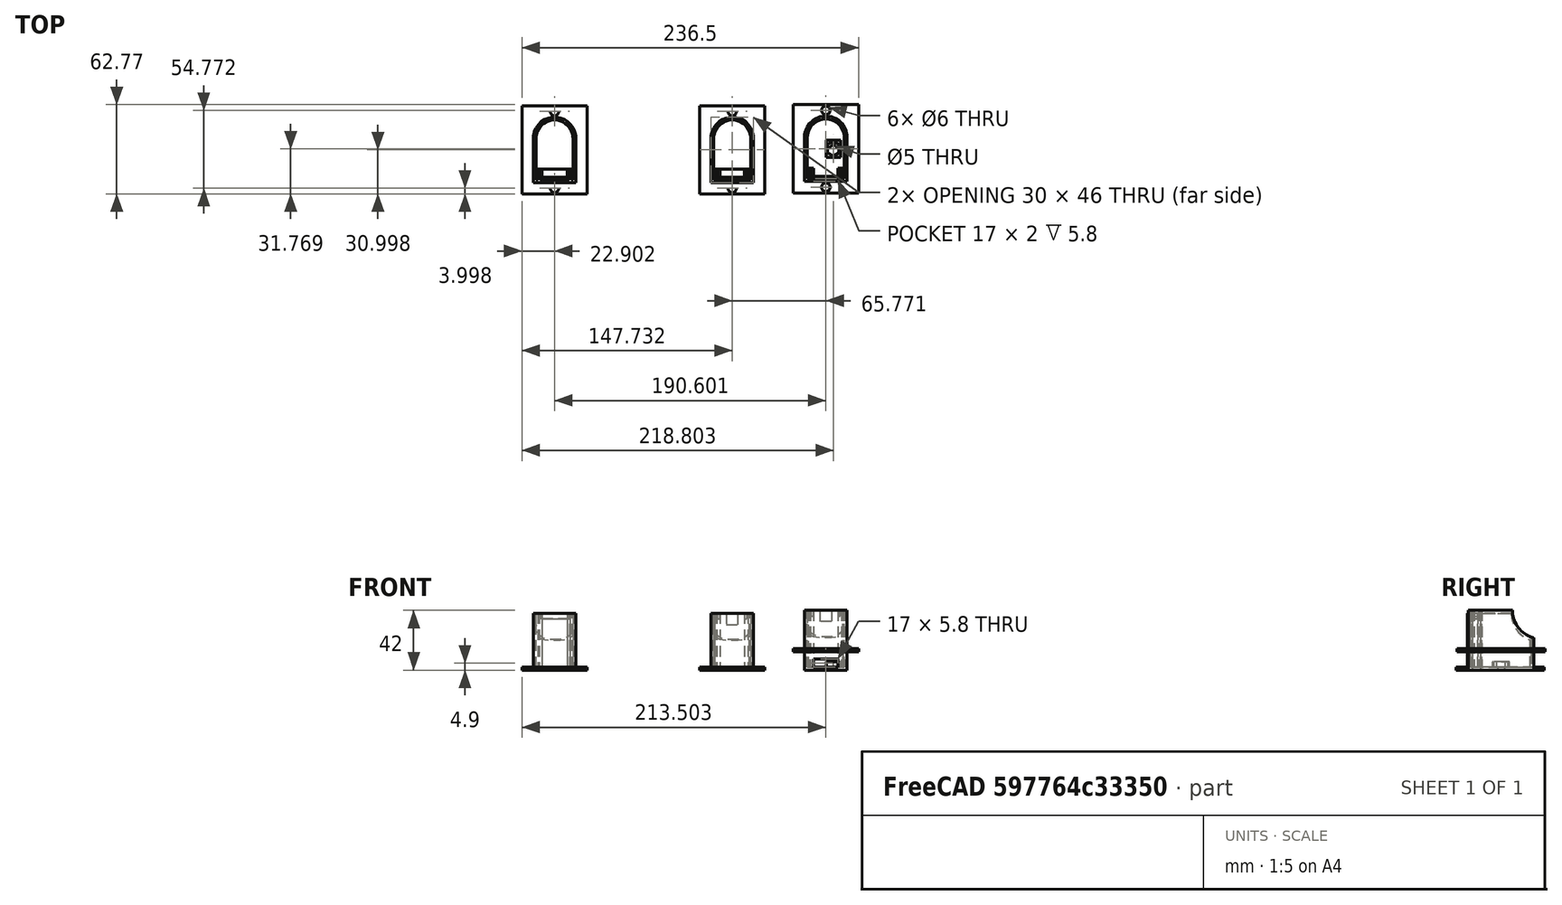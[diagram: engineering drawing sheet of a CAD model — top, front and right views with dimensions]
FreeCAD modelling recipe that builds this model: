
FCSTD DOCUMENT  (FreeCAD 0.18.3R)
Label: lamp.base.nest
License: All rights reserved
LicenseURL: http://en.wikipedia.org/wiki/All_rights_reserved
objects: Part::Extrusion×53, Part::Part2DObjectPython×37, Part::Cut×32, Part::Feature×18, Part::MultiFuse×16, Part::FeaturePython×4
note: 160 computed .brp shape members not serialized (recipe doc carries the construction recipe); baked Part::Feature solids carry a one-line shape summary decoded from their .brp

FEATURE [Part::Part2DObjectPython] Rectangle101  # Draft 2D object (typed FeaturePython)
  ChamferSize = 0
  Columns = 1
  FilletRadius = 0
  Height = 31
  Length = 30
  MakeFace = true
  Placement = pos=(159.976,-36.4369,7.33666) rot=(-1,0,0;2.2e-05rad)
  Rows = 1
FEATURE [Part::Part2DObjectPython] Wire004  # Draft 2D object (typed FeaturePython)
  ChamferSize = 0
  Closed = true
  End = (187.476,-29.036,47.3366)
  FilletRadius = 0
  Length = 82.5995
  MakeFace = true
  Placement = pos=(187.476,-27.0365,47.3366) rot=(1,0,0;3.14159rad)
  Points = (16) [(0,0,0),(-4,-0.000548196,-3.55271e-15),(-4,5.79945,-3.55271e-15),(-21,5.79945,0),(-21,-0.000548196,0),(-25,-0.000548196,3.55271e-15),+10 more]
  Start = (187.476,-27.0365,47.3366)
  Subdivisions = 0
FEATURE [Part::Part2DObjectPython] Circle011  # Draft 2D object (typed FeaturePython)
  FirstAngle = 0
  LastAngle = 0
  MakeFace = true
  Placement = pos=(174.976,-5.43685,7.33598) rot=(-1,0,0;2.2e-05rad)
  Radius = 15
FEATURE [Part::Extrusion] Extrude138
  Base = -> Circle011
  Dir = (0,2.19278e-05,1)
  DirMode = 2
  FaceMakerClass = Part::FaceMakerBullseye
  LengthFwd = 40
  LengthRev = 0
  Solid = false
  Symmetric = false
FEATURE [Part::Extrusion] Extrusion
  Base = -> Wire004
  Dir = (4.1e-15,2.69e-14,-40)
  DirMode = 0
  FaceMakerClass = Part::FaceMakerBullseye
  LengthFwd = 0
  LengthRev = 0
  Solid = true
  Symmetric = false
FEATURE [Part::Part2DObjectPython] Rectangle103  # Draft 2D object (typed FeaturePython)
  ChamferSize = 0
  Columns = 1
  FilletRadius = 0
  Height = 29
  Length = 26
  MakeFace = true
  Placement = pos=(161.976,-34.4369,7.33661) rot=(-1,0,0;2.2e-05rad)
  Rows = 1
FEATURE [Part::Part2DObjectPython] Circle008  # Draft 2D object (typed FeaturePython)
  FirstAngle = 0
  LastAngle = 0
  MakeFace = true
  Placement = pos=(174.976,-5.43685,7.33598) rot=(-1,0,0;2.2e-05rad)
  Radius = 13
FEATURE [Part::Extrusion] Extrude137
  Base = -> Circle008
  Dir = (0,2.19278e-05,1)
  DirMode = 2
  FaceMakerClass = Part::FaceMakerBullseye
  LengthFwd = 40
  LengthRev = 0
  Solid = false
  Symmetric = false
FEATURE [Part::Cut] Cut046
  Base = -> Extrude138
  Tool = -> Extrude137
FEATURE [Part::Extrusion] Extrude136
  Base = -> Rectangle101
  Dir = (0,2.19278e-05,1)
  DirMode = 2
  FaceMakerClass = Part::FaceMakerBullseye
  LengthFwd = 40
  LengthRev = 0
  Solid = false
  Symmetric = false
FEATURE [Part::Extrusion] Extrude129
  Base = -> Rectangle103
  Dir = (0,2.19278e-05,1)
  DirMode = 2
  FaceMakerClass = Part::FaceMakerBullseye
  LengthFwd = 40
  LengthRev = 0
  Solid = false
  Symmetric = false
FEATURE [Part::Cut] Cut045
  Base = -> Extrude136
  Tool = -> Extrude129
FEATURE [Part::Part2DObjectPython] Rectangle102  # Draft 2D object (typed FeaturePython)
  ChamferSize = 0
  Columns = 1
  FilletRadius = 0
  Height = 30
  Length = 40
  MakeFace = true
  Placement = pos=(159.976,-5.43685,7.33598) rot=(0.577354,0.577354,0.577342;4.18878rad)
  Rows = 1
  Support = -> [Cut045]
FEATURE [Part::FeaturePython] Slice001  # WARN: FeaturePython — macro-defined, semantics opaque (R4)
  Base = -> Cut046
  Mode = 1
  Tolerance = 0
  Tools = -> [Rectangle102]
FEATURE [Part::FeaturePython] Slice_child001  label="Slice.001"  # WARN: FeaturePython — macro-defined, semantics opaque (R4)
  Base = -> Slice001
  FilterType = 1
  Invert = false
  OverrideMaxVal = 0
  Placement = pos=(56.3169,21.6057,-20.0005) rot=(0,0,1;0rad)
  WindowFrom = 80
  WindowTo = 100
  items = 0
FEATURE [Part::Part2DObjectPython] Circle012  # Draft 2D object (typed FeaturePython)
  FirstAngle = 0
  LastAngle = 0
  MakeFace = true
  Placement = pos=(159.976,95.9163,14.9502) rot=(0.577346,-0.577359,-0.577346;2.09438rad)
  Radius = 20
  Support = -> [Cut045]
FEATURE [Part::Extrusion] Extrude139
  Base = -> Circle012
  Dir = (-1,-1e-16,1e-16)
  DirMode = 2
  FaceMakerClass = Part::FaceMakerBullseye
  LengthFwd = 50
  LengthRev = 0
  Placement = pos=(106.317,-59.7466,12.3849) rot=(0,0,1;0rad)
  Solid = false
  Symmetric = false
FEATURE [Part::Cut] Cut047
  Base = -> Slice_child001
  Placement = pos=(-56.3169,-21.6057,20.0005) rot=(0,0,1;0rad)
  Tool = -> Extrude139
FEATURE [Part::MultiFuse] Fusion030
  Shapes = -> [Cut045,Cut047]
FEATURE [Part::MultiFuse] Fusion029
  Placement = pos=(-344.724,-139.426,0.00305731) rot=(0,0,1;0rad)
  Shapes = -> [Extrusion,Fusion030]
FEATURE [Part::Part2DObjectPython] Rectangle  # Draft 2D object (typed FeaturePython)
  ChamferSize = 0
  Columns = 1
  FilletRadius = 0
  Height = 8
  Length = 1
  MakeFace = true
  Placement = pos=(-182.748,-173.862,47.3397) rot=(-1,0,0;2.2e-05rad)
  Rows = 1
  Support = -> [Fusion029]
FEATURE [Part::Extrusion] Extrude
  Base = -> Rectangle
  Dir = (0,2.19278e-05,1)
  DirMode = 2
  FaceMakerClass = Part::FaceMakerBullseye
  LengthFwd = -60
  LengthRev = 0
  Placement = pos=(0,0.000219278,10) rot=(0,0,1;0rad)
  Solid = false
  Symmetric = false
FEATURE [Part::Cut] Cut050
  Base = -> Fusion029
  Tool = -> Extrude
FEATURE [Part::Part2DObjectPython] Rectangle105  # Draft 2D object (typed FeaturePython)
  ChamferSize = 0
  Columns = 1
  FilletRadius = 0
  Height = 8
  Length = 1
  MakeFace = true
  Placement = pos=(-157.248,-173.862,47.3397) rot=(-1,0,0;2.2e-05rad)
  Rows = 1
  Support = -> [Cut050]
FEATURE [Part::Extrusion] Extrude144
  Base = -> Rectangle105
  Dir = (0,2.19278e-05,1)
  DirMode = 2
  FaceMakerClass = Part::FaceMakerBullseye
  LengthFwd = -60
  LengthRev = 0
  Placement = pos=(-0.5,0.000219278,10) rot=(0,0,1;0rad)
  Solid = false
  Symmetric = false
FEATURE [Part::Cut] Cut051
  Base = -> Cut050
  Tool = -> Extrude144
FEATURE [Part::Part2DObjectPython] Rectangle106  # Draft 2D object (typed FeaturePython)
  ChamferSize = 0
  Columns = 1
  FilletRadius = 0
  Height = 40
  Length = 2
  MakeFace = true
  Placement = pos=(-157.248,-173.862,7.33967) rot=(0.57735,0.57735,0.57735;2.0944rad)
  Rows = 1
  Support = -> [Cut051]
FEATURE [Part::Extrusion] Extrude145
  Base = -> Rectangle106
  Dir = (1,-7e-16,-7e-16)
  DirMode = 2
  FaceMakerClass = Part::FaceMakerBullseye
  LengthFwd = -0.5
  LengthRev = 0
  Solid = false
  Symmetric = false
FEATURE [Part::Cut] Cut052
  Base = -> Cut051
  Tool = -> Extrude145
FEATURE [Part::Part2DObjectPython] Rectangle107  # Draft 2D object (typed FeaturePython)
  ChamferSize = 0
  Columns = 1
  FilletRadius = 0
  Height = 40
  Length = 2
  MakeFace = true
  Placement = pos=(-182.248,-171.862,7.33967) rot=(0.57735,-0.57735,-0.57735;2.0944rad)
  Rows = 1
  Support = -> [Cut052]
FEATURE [Part::Extrusion] Extrude146
  Base = -> Rectangle107
  Dir = (-1,-2e-16,-3e-16)
  DirMode = 2
  FaceMakerClass = Part::FaceMakerBullseye
  LengthFwd = -0.5
  LengthRev = 0
  Solid = false
  Symmetric = false
FEATURE [Part::Cut] Cut053
  Base = -> Cut052
  Tool = -> Extrude146
FEATURE [Part::Part2DObjectPython] Rectangle108  # Draft 2D object (typed FeaturePython)
  ChamferSize = 0
  Columns = 1
  FilletRadius = 0
  Height = 62
  Length = 46
  MakeFace = true
  Placement = pos=(-192.748,-121.863,7.33853) rot=(1,0,0;3.14157rad)
  Rows = 1
FEATURE [Part::Extrusion] Extrude147
  Base = -> Rectangle108
  Dir = (0,-2.19278e-05,-1)
  DirMode = 2
  FaceMakerClass = Part::FaceMakerBullseye
  LengthFwd = -2
  LengthRev = 0
  Solid = false
  Symmetric = false
FEATURE [Part::Part2DObjectPython] Circle  # Draft 2D object (typed FeaturePython)
  FirstAngle = 0
  LastAngle = 0
  MakeFace = true
  Placement = pos=(-169.748,-125.863,7.33862) rot=(1,0,0;3.14157rad)
  Radius = 3
  Support = -> [Extrude147]
FEATURE [Part::Part2DObjectPython] Circle013  # Draft 2D object (typed FeaturePython)
  FirstAngle = 0
  LastAngle = 0
  MakeFace = true
  Placement = pos=(-169.748,-179.863,7.3398) rot=(1,0,0;3.14157rad)
  Radius = 3
FEATURE [Part::Extrusion] Extrude148
  Base = -> Circle
  Dir = (0,-2.19278e-05,-1)
  DirMode = 2
  FaceMakerClass = Part::FaceMakerBullseye
  LengthFwd = -4
  LengthRev = 0
  Solid = false
  Symmetric = false
FEATURE [Part::Extrusion] Extrude149
  Base = -> Circle013
  Dir = (0,-2.19278e-05,-1)
  DirMode = 2
  FaceMakerClass = Part::FaceMakerBullseye
  LengthFwd = -4
  LengthRev = 0
  Solid = false
  Symmetric = false
FEATURE [Part::Cut] Cut
  Base = -> Extrude147
  Tool = -> Extrude149
FEATURE [Part::Cut] Cut054
  Base = -> Cut
  Tool = -> Extrude148
FEATURE [Part::MultiFuse] Fusion
  Shapes = -> [Cut054,Cut053]
FEATURE [Part::Part2DObjectPython] Rectangle109  # Draft 2D object (typed FeaturePython)
  ChamferSize = 0
  Columns = 1
  FilletRadius = 0
  Height = 5.8
  Length = 17
  MakeFace = true
  Placement = pos=(-178.248,-172.262,9.33964) rot=(-1,0,0;2.2e-05rad)
  Rows = 1
  Support = -> [Fusion]
FEATURE [Part::Extrusion] Extrude150
  Base = -> Rectangle109
  Dir = (0,2.19278e-05,1)
  DirMode = 2
  FaceMakerClass = Part::FaceMakerBullseye
  LengthFwd = -10
  LengthRev = 0
  Solid = false
  Symmetric = false
FEATURE [Part::Cut] Cut055
  Base = -> Fusion
  Tool = -> Extrude150
FEATURE [Part::Part2DObjectPython] Rectangle110  # Draft 2D object (typed FeaturePython)
  ChamferSize = 0
  Columns = 1
  FilletRadius = 0
  Height = 8
  Length = 8
  MakeFace = true
  Placement = pos=(-133.024,-172.269,47.3397) rot=(-1,0,0;1.5708rad)
  Rows = 1
FEATURE [Part::Extrusion] Extrude151
  Base = -> Rectangle110
  Dir = (0,1,7e-16)
  DirMode = 2
  FaceMakerClass = Part::FaceMakerBullseye
  LengthFwd = -1.7
  LengthRev = 0
  Placement = pos=(-40.7237,0.0066316,-3.08384e-05) rot=(0,0,1;0rad)
  Solid = false
  Symmetric = false
FEATURE [Part::Part2DObjectPython] Rectangle111  # Draft 2D object (typed FeaturePython)
  ChamferSize = 0
  Columns = 1
  FilletRadius = 0
  Height = 6.3
  Length = 1.2
  MakeFace = true
  Placement = pos=(-139.224,-173.869,47.3397) rot=(0,0,1;0rad)
  Rows = 1
FEATURE [Part::Feature] Face002
  Placement = pos=(-173.748,-172.262,47.3397) rot=(-1,0,0;1.5708rad)
  shape: bbox 8 x 2e-07 x 8 mm, 1 faces, 0 solids (baked)
FEATURE [Part::Feature] Face004
  shape: bbox 8 x 3.49 x 4.243e-07 mm, 1 faces, 0 solids (baked)
FEATURE [Part::Feature] Face005
  shape: bbox 8 x 1.7 x 2e-07 mm, 1 faces, 0 solids (baked)
FEATURE [Part::Extrusion] Extrude152
  Base = -> Rectangle111
  Dir = (0,-8e-16,1)
  DirMode = 2
  FaceMakerClass = Part::FaceMakerBullseye
  LengthFwd = -4
  LengthRev = 0
  Placement = pos=(-40.7237,0.0066316,-3.08384e-05) rot=(0,0,1;0rad)
  Solid = false
  Symmetric = false
FEATURE [Part::Part2DObjectPython] Rectangle112  # Draft 2D object (typed FeaturePython)
  ChamferSize = 0
  Columns = 1
  FilletRadius = 0
  Height = 6.3
  Length = 1.2
  MakeFace = true
  Placement = pos=(-120.024,-173.869,47.3397) rot=(0,0,1;0rad)
  Rows = 1
FEATURE [Part::Extrusion] Extrude153
  Base = -> Rectangle112
  Dir = (0,-8e-16,1)
  DirMode = 2
  FaceMakerClass = Part::FaceMakerBullseye
  LengthFwd = -4
  LengthRev = 0
  Placement = pos=(-40.7237,0.0066316,-3.08384e-05) rot=(0,0,1;0rad)
  Solid = false
  Symmetric = false
FEATURE [Part::Extrusion] Extrusion004
  Base = -> Face002
  Dir = (1e-16,3.49022,2.7e-15)
  DirMode = 0
  FaceMakerClass = Part::FaceMakerBullseye
  LengthFwd = 0
  LengthRev = 0
  Solid = true
  Symmetric = false
FEATURE [Part::MultiFuse] Fusion032
  Shapes = -> [Extrusion004,Extrude151]
FEATURE [Part::Extrusion] Extrusion005
  Base = -> Face004
  Dir = (3e-16,-7.8e-15,10.0677)
  DirMode = 0
  FaceMakerClass = Part::FaceMakerBullseye
  LengthFwd = 0
  LengthRev = 0
  Solid = true
  Symmetric = false
FEATURE [Part::Extrusion] Extrusion006
  Base = -> Face005
  Dir = (3e-16,-7.3e-15,10.0677)
  DirMode = 0
  FaceMakerClass = Part::FaceMakerBullseye
  LengthFwd = 0
  LengthRev = 0
  Solid = true
  Symmetric = false
FEATURE [Part::MultiFuse] Fusion033
  Shapes = -> [Fusion032,Extrusion006,Extrusion005]
FEATURE [Part::MultiFuse] Fusion034
  Shapes = -> [Fusion033,Extrude153,Extrude152]
FEATURE [Part::Cut] Cut056
  Base = -> Cut055
  Placement = pos=(-6.0896,-2.3491,-1.99694) rot=(0,0,1;0rad)
  Tool = -> Fusion034
FEATURE [Part::Part2DObjectPython] Wire005  # Draft 2D object (typed FeaturePython)
  ChamferSize = 0
  Closed = true
  End = (187.476,-29.036,47.3366)
  FilletRadius = 0
  Length = 82.5995
  MakeFace = true
  Placement = pos=(187.476,-27.0365,47.3366) rot=(1,0,0;3.14159rad)
  Points = (16) [(0,0,0),(-4,-0.000548196,-3.55271e-15),(-4,5.79945,-3.55271e-15),(-21,5.79945,0),(-21,-0.000548196,0),(-25,-0.000548196,3.55271e-15),+10 more]
  Start = (187.476,-27.0365,47.3366)
  Subdivisions = 0
FEATURE [Part::Part2DObjectPython] Circle014  # Draft 2D object (typed FeaturePython)
  FirstAngle = 0
  LastAngle = 0
  MakeFace = true
  Placement = pos=(174.976,-5.43685,7.33598) rot=(-1,0,0;2.2e-05rad)
  Radius = 15
FEATURE [Part::Extrusion] Extrude154
  Base = -> Circle014
  Dir = (0,2.19278e-05,1)
  DirMode = 2
  FaceMakerClass = Part::FaceMakerBullseye
  LengthFwd = 40
  LengthRev = 0
  Solid = false
  Symmetric = false
FEATURE [Part::Part2DObjectPython] Circle015  # Draft 2D object (typed FeaturePython)
  FirstAngle = 0
  LastAngle = 0
  MakeFace = true
  Placement = pos=(174.976,-5.43685,7.33598) rot=(-1,0,0;2.2e-05rad)
  Radius = 13
FEATURE [Part::Part2DObjectPython] Rectangle118  # Draft 2D object (typed FeaturePython)
  ChamferSize = 0
  Columns = 1
  FilletRadius = 0
  Height = 29
  Length = 26
  MakeFace = true
  Placement = pos=(161.976,-34.4369,7.33661) rot=(-1,0,0;2.2e-05rad)
  Rows = 1
FEATURE [Part::Extrusion] Extrusion023
  Base = -> Wire005
  Dir = (4.1e-15,2.69e-14,-40)
  DirMode = 0
  FaceMakerClass = Part::FaceMakerBullseye
  LengthFwd = 0
  LengthRev = 0
  Solid = true
  Symmetric = false
FEATURE [Part::Extrusion] Extrude178
  Base = -> Circle015
  Dir = (0,2.19278e-05,1)
  DirMode = 2
  FaceMakerClass = Part::FaceMakerBullseye
  LengthFwd = 40
  LengthRev = 0
  Solid = false
  Symmetric = false
FEATURE [Part::Cut] Cut062
  Base = -> Extrude154
  Tool = -> Extrude178
FEATURE [Part::Extrusion] Extrude179
  Base = -> Rectangle118
  Dir = (0,2.19278e-05,1)
  DirMode = 2
  FaceMakerClass = Part::FaceMakerBullseye
  LengthFwd = 40
  LengthRev = 0
  Solid = false
  Symmetric = false
FEATURE [Part::Part2DObjectPython] Rectangle119  # Draft 2D object (typed FeaturePython)
  ChamferSize = 0
  Columns = 1
  FilletRadius = 0
  Height = 31
  Length = 30
  MakeFace = true
  Placement = pos=(159.976,-36.4369,7.33666) rot=(-1,0,0;2.2e-05rad)
  Rows = 1
FEATURE [Part::Extrusion] Extrude176
  Base = -> Rectangle119
  Dir = (0,2.19278e-05,1)
  DirMode = 2
  FaceMakerClass = Part::FaceMakerBullseye
  LengthFwd = 40
  LengthRev = 0
  Solid = false
  Symmetric = false
FEATURE [Part::Cut] Cut061
  Base = -> Extrude176
  Tool = -> Extrude179
FEATURE [Part::Part2DObjectPython] Rectangle117  # Draft 2D object (typed FeaturePython)
  ChamferSize = 0
  Columns = 1
  FilletRadius = 0
  Height = 30
  Length = 40
  MakeFace = true
  Placement = pos=(159.976,-5.43685,7.33598) rot=(0.577354,0.577354,0.577342;4.18878rad)
  Rows = 1
  Support = -> [Cut061]
FEATURE [Part::FeaturePython] Slice002  # WARN: FeaturePython — macro-defined, semantics opaque (R4)
  Base = -> Cut062
  Mode = 1
  Tolerance = 0
  Tools = -> [Rectangle117]
FEATURE [Part::FeaturePython] Slice_child002  label="Slice.002"  # WARN: FeaturePython — macro-defined, semantics opaque (R4)
  Base = -> Slice002
  FilterType = 1
  Invert = false
  OverrideMaxVal = 0
  Placement = pos=(56.3169,21.6057,-20.0005) rot=(0,0,1;0rad)
  WindowFrom = 80
  WindowTo = 100
  items = 0
FEATURE [Part::Part2DObjectPython] Circle016  # Draft 2D object (typed FeaturePython)
  FirstAngle = 0
  LastAngle = 0
  MakeFace = true
  Placement = pos=(159.976,95.9163,14.9502) rot=(0.577346,-0.577359,-0.577346;2.09438rad)
  Radius = 20
  Support = -> [Cut061]
FEATURE [Part::Extrusion] Extrude155
  Base = -> Circle016
  Dir = (-1,-1e-16,1e-16)
  DirMode = 2
  FaceMakerClass = Part::FaceMakerBullseye
  LengthFwd = 50
  LengthRev = 0
  Placement = pos=(106.317,-59.7466,12.3849) rot=(0,0,1;0rad)
  Solid = false
  Symmetric = false
FEATURE [Part::Cut] Cut063
  Base = -> Slice_child002
  Placement = pos=(-56.3169,-21.6057,20.0005) rot=(0,0,1;0rad)
  Tool = -> Extrude155
FEATURE [Part::MultiFuse] Fusion031
  Shapes = -> [Cut061,Cut063]
FEATURE [Part::MultiFuse] Fusion036
  Placement = pos=(-344.724,-139.426,0.00305731) rot=(0,0,1;0rad)
  Shapes = -> [Extrusion023,Fusion031]
FEATURE [Part::Part2DObjectPython] Rectangle114  # Draft 2D object (typed FeaturePython)
  ChamferSize = 0
  Columns = 1
  FilletRadius = 0
  Height = 8
  Length = 1
  MakeFace = true
  Placement = pos=(-182.748,-173.862,47.3397) rot=(-1,0,0;2.2e-05rad)
  Rows = 1
  Support = -> [Fusion036]
FEATURE [Part::Extrusion] Extrude174
  Base = -> Rectangle114
  Dir = (0,2.19278e-05,1)
  DirMode = 2
  FaceMakerClass = Part::FaceMakerBullseye
  LengthFwd = -60
  LengthRev = 0
  Placement = pos=(0,0.000219278,10) rot=(0,0,1;0rad)
  Solid = false
  Symmetric = false
FEATURE [Part::Cut] Cut059
  Base = -> Fusion036
  Tool = -> Extrude174
FEATURE [Part::Part2DObjectPython] Rectangle116  # Draft 2D object (typed FeaturePython)
  ChamferSize = 0
  Columns = 1
  FilletRadius = 0
  Height = 8
  Length = 1
  MakeFace = true
  Placement = pos=(-157.248,-173.862,47.3397) rot=(-1,0,0;2.2e-05rad)
  Rows = 1
  Support = -> [Cut059]
FEATURE [Part::Extrusion] Extrude173
  Base = -> Rectangle116
  Dir = (0,2.19278e-05,1)
  DirMode = 2
  FaceMakerClass = Part::FaceMakerBullseye
  LengthFwd = -60
  LengthRev = 0
  Placement = pos=(-0.5,0.000219278,10) rot=(0,0,1;0rad)
  Solid = false
  Symmetric = false
FEATURE [Part::Cut] Cut058
  Base = -> Cut059
  Tool = -> Extrude173
FEATURE [Part::Part2DObjectPython] Rectangle115  # Draft 2D object (typed FeaturePython)
  ChamferSize = 0
  Columns = 1
  FilletRadius = 0
  Height = 40
  Length = 2
  MakeFace = true
  Placement = pos=(-157.248,-173.862,7.33967) rot=(0.57735,0.57735,0.57735;2.0944rad)
  Rows = 1
  Support = -> [Cut058]
FEATURE [Part::Extrusion] Extrude175
  Base = -> Rectangle115
  Dir = (1,-7e-16,-7e-16)
  DirMode = 2
  FaceMakerClass = Part::FaceMakerBullseye
  LengthFwd = -0.5
  LengthRev = 0
  Solid = false
  Symmetric = false
FEATURE [Part::Cut] Cut057
  Base = -> Cut058
  Tool = -> Extrude175
FEATURE [Part::Part2DObjectPython] Rectangle113  # Draft 2D object (typed FeaturePython)
  ChamferSize = 0
  Columns = 1
  FilletRadius = 0
  Height = 40
  Length = 2
  MakeFace = true
  Placement = pos=(-182.248,-171.862,7.33967) rot=(0.57735,-0.57735,-0.57735;2.0944rad)
  Rows = 1
  Support = -> [Cut057]
FEATURE [Part::Extrusion] Extrude177
  Base = -> Rectangle113
  Dir = (-1,-2e-16,-3e-16)
  DirMode = 2
  FaceMakerClass = Part::FaceMakerBullseye
  LengthFwd = -0.5
  LengthRev = 0
  Solid = false
  Symmetric = false
FEATURE [Part::Cut] Cut060
  Base = -> Cut057
  Placement = pos=(418.796,148.561,-0.00325763) rot=(0,0,1;0rad)
  Tool = -> Extrude177
FEATURE [Part::Part2DObjectPython] Rectangle123  # Draft 2D object (typed FeaturePython)
  ChamferSize = 0
  Columns = 1
  FilletRadius = 0
  Height = 8
  Length = 8
  MakeFace = true
  Placement = pos=(-133.024,-172.269,47.3397) rot=(-1,0,0;1.5708rad)
  Rows = 1
FEATURE [Part::Extrusion] Extrude172
  Base = -> Rectangle123
  Dir = (0,1,1.1e-15)
  DirMode = 2
  FaceMakerClass = Part::FaceMakerBullseye
  LengthFwd = -1.7
  LengthRev = 0
  Placement = pos=(-40.7237,0.0066316,-3.08384e-05) rot=(0,0,1;0rad)
  Solid = false
  Symmetric = false
FEATURE [Part::Feature] Face006
  Placement = pos=(-173.748,-172.262,47.3397) rot=(-1,0,0;1.5708rad)
  shape: bbox 8 x 2e-07 x 8 mm, 1 faces, 0 solids (baked)
FEATURE [Part::Extrusion] Extrusion024
  Base = -> Face006
  Dir = (1e-16,3.49022,2.7e-15)
  DirMode = 0
  FaceMakerClass = Part::FaceMakerBullseye
  LengthFwd = 0
  LengthRev = 0
  Solid = true
  Symmetric = false
FEATURE [Part::MultiFuse] Fusion037
  Shapes = -> [Extrusion024,Extrude172]
FEATURE [Part::Part2DObjectPython] Rectangle122  # Draft 2D object (typed FeaturePython)
  ChamferSize = 0
  Columns = 1
  FilletRadius = 0
  Height = 6.3
  Length = 1.2
  MakeFace = true
  Placement = pos=(-139.224,-173.869,47.3397) rot=(0,0,1;0rad)
  Rows = 1
FEATURE [Part::Extrusion] Extrude171
  Base = -> Rectangle122
  Dir = (0,-1e-15,1)
  DirMode = 2
  FaceMakerClass = Part::FaceMakerBullseye
  LengthFwd = -4
  LengthRev = 0
  Placement = pos=(-40.7237,0.0066316,-3.08384e-05) rot=(0,0,1;0rad)
  Solid = false
  Symmetric = false
FEATURE [Part::Part2DObjectPython] Rectangle124  # Draft 2D object (typed FeaturePython)
  ChamferSize = 0
  Columns = 1
  FilletRadius = 0
  Height = 6.3
  Length = 1.2
  MakeFace = true
  Placement = pos=(-120.024,-173.869,47.3397) rot=(0,0,1;0rad)
  Rows = 1
FEATURE [Part::Extrusion] Extrude180
  Base = -> Rectangle124
  Dir = (0,-8e-16,1)
  DirMode = 2
  FaceMakerClass = Part::FaceMakerBullseye
  LengthFwd = -4
  LengthRev = 0
  Placement = pos=(-40.7237,0.0066316,-3.08384e-05) rot=(0,0,1;0rad)
  Solid = false
  Symmetric = false
FEATURE [Part::MultiFuse] Fusion035
  Placement = pos=(418.796,148.561,-0.00325763) rot=(0,0,1;0rad)
  Shapes = -> [Extrude171,Extrude180,Fusion037]
FEATURE [Part::Cut] Cut071
  Base = -> Cut060
  Placement = pos=(-359.114,-150.139,0.00329223) rot=(0,0,1;0rad)
  Tool = -> Fusion035
FEATURE [Part::Part2DObjectPython] Rectangle125  # Draft 2D object (typed FeaturePython)
  ChamferSize = 0
  Columns = 1
  FilletRadius = 0
  Height = 31
  Length = 30
  MakeFace = true
  Placement = pos=(-125.067,-146.441,7.33907) rot=(1,0,0;3.14157rad)
  Rows = 1
FEATURE [Part::Part2DObjectPython] Circle017  # Draft 2D object (typed FeaturePython)
  FirstAngle = 0
  LastAngle = 0
  MakeFace = true
  Placement = pos=(-110.067,-146.441,7.33907) rot=(1,0,0;3.14157rad)
  Radius = 15
FEATURE [Part::Extrusion] Extrude181
  Base = -> Rectangle125
  Dir = (0,-2.19278e-05,-1)
  DirMode = 2
  FaceMakerClass = Part::FaceMakerBullseye
  LengthFwd = 2
  LengthRev = 0
  Solid = false
  Symmetric = false
FEATURE [Part::Extrusion] Extrude182
  Base = -> Circle017
  Dir = (0,-2.19278e-05,-1)
  DirMode = 2
  FaceMakerClass = Part::FaceMakerBullseye
  LengthFwd = 2
  LengthRev = 0
  Solid = false
  Symmetric = false
FEATURE [Part::MultiFuse] Fusion038
  Shapes = -> [Extrude182,Extrude181]
FEATURE [Part::Part2DObjectPython] Rectangle126  # Draft 2D object (typed FeaturePython)
  ChamferSize = 0
  Columns = 1
  FilletRadius = 0
  Height = 5.79984
  Length = 17
  MakeFace = true
  Placement = pos=(-118.567,-173.84,13.1397) rot=(-1,0,0;1.5708rad)
  Rows = 1
  Support = -> [Cut071]
FEATURE [Part::Extrusion] Extrude183
  Base = -> Rectangle126
  Dir = (1e-16,1,7e-16)
  DirMode = 2
  FaceMakerClass = Part::FaceMakerBullseye
  LengthFwd = -5
  LengthRev = 0
  Solid = false
  Symmetric = false
FEATURE [Part::Cut] Cut072
  Base = -> Cut071
  Tool = -> Extrude183
FEATURE [Part::MultiFuse] Fusion039
  Shapes = -> [Fusion038,Cut072]
FEATURE [Part::Part2DObjectPython] Circle019  # Draft 2D object (typed FeaturePython)
  FirstAngle = 0
  LastAngle = 0
  MakeFace = true
  Placement = pos=(-104.767,-154.441,5.33925) rot=(0,1,-1.1e-05;3.14159rad)
  Radius = 2.5
FEATURE [Part::Extrusion] Extrude184
  Base = -> Circle019
  Dir = (0,-2.19278e-05,-1)
  DirMode = 2
  FaceMakerClass = Part::FaceMakerBullseye
  LengthFwd = -5
  LengthRev = 0
  Solid = false
  Symmetric = false
FEATURE [Part::Cut] Cut073
  Base = -> Fusion039
  Tool = -> Extrude184
FEATURE [Part::Part2DObjectPython] Rectangle127  # Draft 2D object (typed FeaturePython)
  ChamferSize = 0
  Columns = 1
  FilletRadius = 0
  Height = 12
  Length = 10
  MakeFace = true
  Placement = pos=(-109.767,-160.441,7.33938) rot=(-1,0,0;2.2e-05rad)
  Rows = 1
  Support = -> [Cut073]
FEATURE [Part::Extrusion] Extrude185
  Base = -> Wire005
  Dir = (-1e-16,5e-16,1)
  DirMode = 2
  FaceMakerClass = Part::FaceMakerBullseye
  LengthFwd = 4
  LengthRev = 0
  Solid = false
  Symmetric = false
FEATURE [Part::Feature] Face
  Placement = pos=(-176.23,-311.495,10) rot=(0,0,1;0rad)
  shape: bbox 8 x 10 x 2e-07 mm, 1 faces, 0 solids (baked)
FEATURE [Part::Extrusion] Extrusion025
  Base = -> Face
  Dir = (-3e-16,0,1)
  DirMode = 0
  FaceMakerClass = Part::FaceMakerBullseye
  LengthFwd = 0
  LengthRev = 0
  Solid = true
  Symmetric = false
FEATURE [Part::MultiFuse] Fusion040
  Placement = pos=(71.463,162.054,1.33925) rot=(0,0,1;0rad)
  Shapes = -> [Extrusion025,Extrude185]
FEATURE [Part::Extrusion] Extrude186
  Base = -> Rectangle127
  Dir = (0,2.19278e-05,1)
  DirMode = 2
  FaceMakerClass = Part::FaceMakerBullseye
  LengthFwd = 4
  LengthRev = 0
  Solid = false
  Symmetric = false
FEATURE [Part::Feature] Face007
  Placement = pos=(-104.767,-149.441,7.33925) rot=(0,0,1;0rad)
  shape: bbox 8 x 10 x 2e-07 mm, 1 faces, 0 solids (baked)
FEATURE [Part::Extrusion] Extrusion026
  Base = -> Face007
  Dir = (3e-16,0,-1)
  DirMode = 0
  FaceMakerClass = Part::FaceMakerBullseye
  LengthFwd = 0
  LengthRev = 0
  Solid = true
  Symmetric = false
FEATURE [Part::MultiFuse] Fusion041
  Shapes = -> [Fusion040,Extrusion026]
FEATURE [Part::Cut] Cut074
  Base = -> Extrude186
  Tool = -> Fusion041
FEATURE [Part::MultiFuse] Fusion042
  Shapes = -> [Cut074,Cut073]
FEATURE [Part::Feature] Face008
  shape: bbox 46 x 62 x 0.00136 mm, 1 faces, 0 solids (baked)
FEATURE [Part::Extrusion] Extrusion027
  Base = -> Face008
  Dir = (0,-4.37897e-05,-1.99699)
  DirMode = 0
  FaceMakerClass = Part::FaceMakerBullseye
  LengthFwd = 0
  LengthRev = 0
  Placement = pos=(59.6813,-1.57757,12.997) rot=(0,0,1;0rad)
  Solid = true
  Symmetric = false
FEATURE [Part::MultiFuse] Fusion043
  Shapes = -> [Extrusion027,Fusion042]
FEATURE [Part::Feature] Fusion044007_solid001  label="Fusion044007 (Solid)001"
  Placement = pos=(-62.1763,0,0) rot=(0,0,1;0rad)
  shape: bbox 46 x 62 x 40 mm, 59 faces (baked)
FEATURE [Part::Feature] Face014
  Placement = pos=(-62.1763,0,0) rot=(0,0,1;0rad)
  shape: bbox 6.926e-07 x 2 x 38 mm, 1 faces, 0 solids (baked)
FEATURE [Part::Extrusion] Extrusion035
  Base = -> Face014
  Dir = (0.2,0,0)
  DirMode = 0
  FaceMakerClass = Part::FaceMakerBullseye
  LengthFwd = 0
  LengthRev = 0
  Solid = true
  Symmetric = false
FEATURE [Part::Feature] Face015
  Placement = pos=(-62.1763,0,0) rot=(0,0,1;0rad)
  shape: bbox 7.002e-06 x 2 x 38 mm, 1 faces, 0 solids (baked)
FEATURE [Part::Extrusion] Extrusion036
  Base = -> Face015
  Dir = (0.2,0,0)
  DirMode = 0
  FaceMakerClass = Part::FaceMakerBullseye
  LengthFwd = 0
  LengthRev = 0
  Solid = true
  Symmetric = false
FEATURE [Part::Feature] Face016
  Placement = pos=(-62.1763,0,0) rot=(0,0,1;0rad)
  shape: bbox 6.926e-07 x 2 x 38 mm, 1 faces, 0 solids (baked)
FEATURE [Part::Extrusion] Extrusion037
  Base = -> Face016
  Dir = (-0.2,0,0)
  DirMode = 0
  FaceMakerClass = Part::FaceMakerBullseye
  LengthFwd = 0
  LengthRev = 0
  Solid = true
  Symmetric = false
FEATURE [Part::Feature] Face017
  Placement = pos=(-62.1763,0,0) rot=(0,0,1;0rad)
  shape: bbox 6.926e-07 x 2 x 38 mm, 1 faces, 0 solids (baked)
FEATURE [Part::Extrusion] Extrusion038
  Base = -> Face017
  Dir = (-0.2,0,0)
  DirMode = 0
  FaceMakerClass = Part::FaceMakerBullseye
  LengthFwd = 0
  LengthRev = 0
  Solid = true
  Symmetric = false
FEATURE [Part::Cut] Cut081
  Base = -> Fusion044007_solid001
  Tool = -> Extrusion038
FEATURE [Part::Cut] Cut082
  Base = -> Cut081
  Tool = -> Extrusion037
FEATURE [Part::Cut] Cut083
  Base = -> Cut082
  Tool = -> Extrusion036
FEATURE [Part::Cut] Cut084
  Base = -> Cut083
  Tool = -> Extrusion035
FEATURE [Part::Feature] Face021
  Placement = pos=(-62.1763,0,0) rot=(0,0,1;0rad)
  shape: bbox 6.926e-07 x 3.4 x 38 mm, 1 faces, 0 solids (baked)
FEATURE [Part::Extrusion] Extrusion042
  Base = -> Face021
  Dir = (0.4,0,-2e-16)
  DirMode = 0
  FaceMakerClass = Part::FaceMakerBullseye
  LengthFwd = 0
  LengthRev = 0
  Solid = true
  Symmetric = false
FEATURE [Part::Feature] Face022
  Placement = pos=(-62.1763,0,0) rot=(0,0,1;0rad)
  shape: bbox 6.926e-07 x 3.4 x 38 mm, 1 faces, 0 solids (baked)
FEATURE [Part::Extrusion] Extrusion043
  Base = -> Face022
  Dir = (-0.40609,0,2e-16)
  DirMode = 0
  FaceMakerClass = Part::FaceMakerBullseye
  LengthFwd = 0
  LengthRev = 0
  Solid = true
  Symmetric = false
FEATURE [Part::Cut] Cut085
  Base = -> Cut084
  Tool = -> Extrusion042
FEATURE [Part::Cut] Cut086
  Base = -> Cut085
  Tool = -> Extrusion043
FEATURE [Part::Feature] Face023
  Placement = pos=(-130.92,-2.3491,-1.99694) rot=(0,0,1;0rad)
  shape: bbox 2e-07 x 62 x 2.001 mm, 1 faces, 0 solids (baked)
FEATURE [Part::Extrusion] Extrusion044
  Base = -> Face023
  Dir = (-0.1,0,0)
  DirMode = 0
  FaceMakerClass = Part::FaceMakerBullseye
  LengthFwd = 0
  LengthRev = 0
  Solid = true
  Symmetric = false
FEATURE [Part::Feature] Face024
  Placement = pos=(-130.92,-2.3491,-1.99694) rot=(0,0,1;0rad)
  shape: bbox 2e-07 x 62 x 2.001 mm, 1 faces, 0 solids (baked)
FEATURE [Part::Extrusion] Extrusion045
  Base = -> Face024
  Dir = (0.1,0,0)
  DirMode = 0
  FaceMakerClass = Part::FaceMakerBullseye
  LengthFwd = 0
  LengthRev = 0
  Solid = true
  Symmetric = false
FEATURE [Part::Feature] Face025
  Placement = pos=(-130.92,-2.3491,-1.99694) rot=(0,0,1;0rad)
  shape: bbox 46 x 4.406e-05 x 2 mm, 1 faces, 0 solids (baked)
FEATURE [Part::Extrusion] Extrusion046
  Base = -> Face025
  Dir = (0,-0.1,2.19278e-06)
  DirMode = 0
  FaceMakerClass = Part::FaceMakerBullseye
  LengthFwd = 0
  LengthRev = 0
  Solid = true
  Symmetric = false
FEATURE [Part::Feature] Face026
  Placement = pos=(-130.92,-2.3491,-1.99694) rot=(0,0,1;0rad)
  shape: bbox 46 x 4.406e-05 x 2 mm, 1 faces, 0 solids (baked)
FEATURE [Part::Extrusion] Extrusion047
  Base = -> Face026
  Dir = (0,0.1,-2.19278e-06)
  DirMode = 0
  FaceMakerClass = Part::FaceMakerBullseye
  LengthFwd = 0
  LengthRev = 0
  Solid = true
  Symmetric = false
FEATURE [Part::Cut] Cut087
  Base = -> Cut086
  Tool = -> Extrusion047
FEATURE [Part::Cut] Cut088
  Base = -> Cut087
  Tool = -> Extrusion046
FEATURE [Part::Cut] Cut089
  Base = -> Cut088
  Tool = -> Extrusion045
FEATURE [Part::Cut] Cut090
  Base = -> Cut089
  Tool = -> Extrusion044
